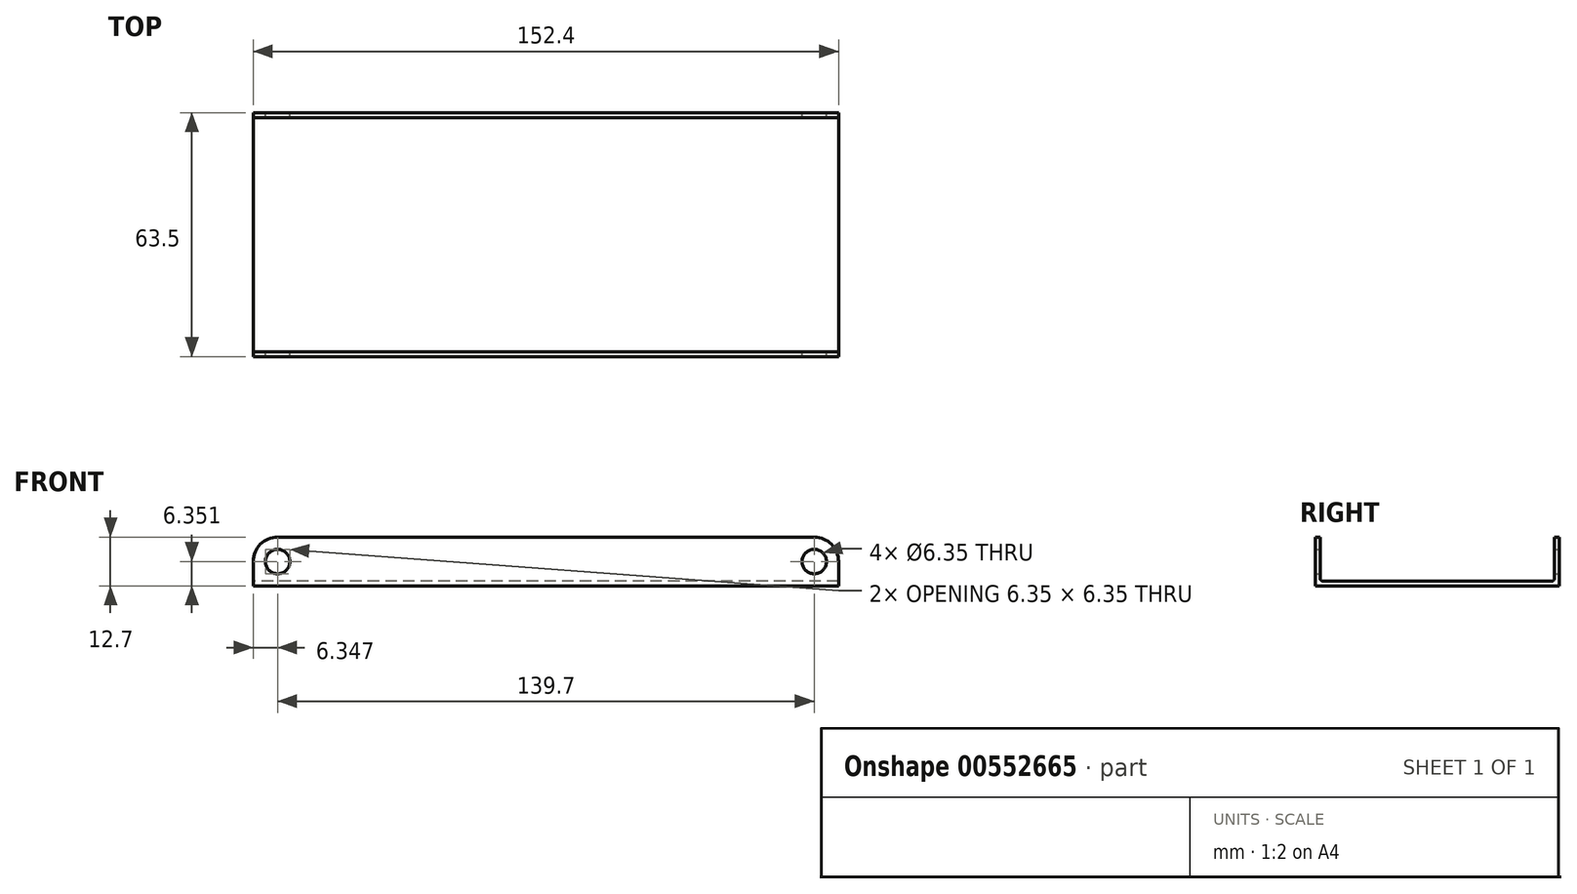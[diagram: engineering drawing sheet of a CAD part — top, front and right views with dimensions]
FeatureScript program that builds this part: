
annotation { "Feature Type Name" : "Feature", "Feature Type Description" : "" }
export const myFeature = defineFeature(function(context is Context, id is Id, definition is map)
    precondition{}
    {
        {
            var Q0;
            Q0=qCreatedBy(makeId("Front.planeOp"),FACE);
            var sketch = newSketch(context, id + "F0", { "sketchPlane" : qUnion([Q0])});
            skLineSegment(sketch, "E0.bottom", {"start": v(-69.48, -6.47) * mm, "end": v(70.22, -6.47) * mm});
            skLineSegment(sketch, "E0.top", {"start": v(-75.83, -19.17) * mm, "end": v(76.57, -19.17) * mm});
            skLineSegment(sketch, "E0.left", {"start": v(-75.83, -12.82) * mm, "end": v(-75.83, -19.17) * mm});
            skLineSegment(sketch, "E0.right", {"start": v(76.57, -12.82) * mm, "end": v(76.57, -19.17) * mm});
            skPoint(sketch, "E1.visualSharp", {"position": v(-75.83, -6.47) * mm});
            skArc(sketch, "E1.filletArc", {"start": v(-69.48, -6.47) * mm, "mid": v(-73.97, -8.33) * mm, "end": v(-75.83, -12.82) * mm});
            skPoint(sketch, "E2.visualSharp", {"position": v(76.57, -6.47) * mm});
            skArc(sketch, "E2.filletArc", {"start": v(76.57, -12.82) * mm, "mid": v(74.7, -8.33) * mm, "end": v(70.22, -6.47) * mm});
            skCircle(sketch, "E3", {"center": v(-69.48, -12.82) * mm, "radius": 3.18 * mm});
            skCircle(sketch, "E4", {"center": v(70.22, -12.82) * mm, "radius": 3.18 * mm});
            skSolve(sketch);
        }
        {
            var Q0;
            Q0 = qSketchRegion(id + "F0", true);
            extrude(context, id + "F1", {"entities" : qUnion([Q0]), "depth" : 63.5 * mm, "offsetDistance" : 25.4 * mm});
        }
        {
            var Q0;
            Q0=makeQuery(id+"F1.opExtrude","SWEPT_FACE",FACE,{"disambiguationData":[OSD([sQuery(id+"F0.wireOp",EDGE,"E0.left")])]});
            var sketch = newSketch(context, id + "F2", { "sketchPlane" : qUnion([Q0])});
            skPoint(sketch, "E5.oppositeSnap0", {"position": v(63.5, -16) * mm});
            skLineSegment(sketch, "E5.bottom", {"start": v(1.27, 9.05) * mm, "end": v(62.23, 9.05) * mm});
            skLineSegment(sketch, "E5.top", {"start": v(1.9, -17.9) * mm, "end": v(61.6, -17.9) * mm});
            skLineSegment(sketch, "E5.left", {"start": v(1.27, 9.05) * mm, "end": v(1.27, -17.26) * mm});
            skLineSegment(sketch, "E5.right", {"start": v(62.23, 9.05) * mm, "end": v(62.23, -17.26) * mm});
            skPoint(sketch, "E6.visualSharp", {"position": v(1.27, -17.9) * mm});
            skArc(sketch, "E6.filletArc", {"start": v(1.27, -17.26) * mm, "mid": v(1.46, -17.71) * mm, "end": v(1.9, -17.9) * mm});
            skPoint(sketch, "E7.visualSharp", {"position": v(62.23, -17.9) * mm});
            skArc(sketch, "E7.filletArc", {"start": v(61.6, -17.9) * mm, "mid": v(62.04, -17.71) * mm, "end": v(62.23, -17.26) * mm});
            skSolve(sketch);
        }
        {
            var Q0;
            {var subQ0=sQuery(id+"F2.wireOp",EDGE,"E5.bottom");Q0=makeQuery(id+"F2.imprint","IMPRINT",FACE,{"disambiguationData":[TD([[makeQuery(id+"F2.imprint","IMPRINT",EDGE,{"derivedFrom":subQ0}),-1.0]])]});}
            var Q1;
            Q1=makeQuery(id+"F2.imprint","IMPRINT",FACE,{"disambiguationData":[TD([[makeQuery(id+"F2.imprint","IMPRINT",EDGE,{"derivedFrom":sQuery(id+"F2.wireOp",EDGE,"E5.top")}),1.0]])]});
            extrude(context, id + "F3", {"entities" : qUnion([Q0, Q1]), "operationType" : NewBodyOperationType.REMOVE, "endBound" : BoundingType.THROUGH_ALL, "oppositeDirection" : true, "depth" : 25.4 * mm, "offsetDistance" : 25.4 * mm});
        }
    });
